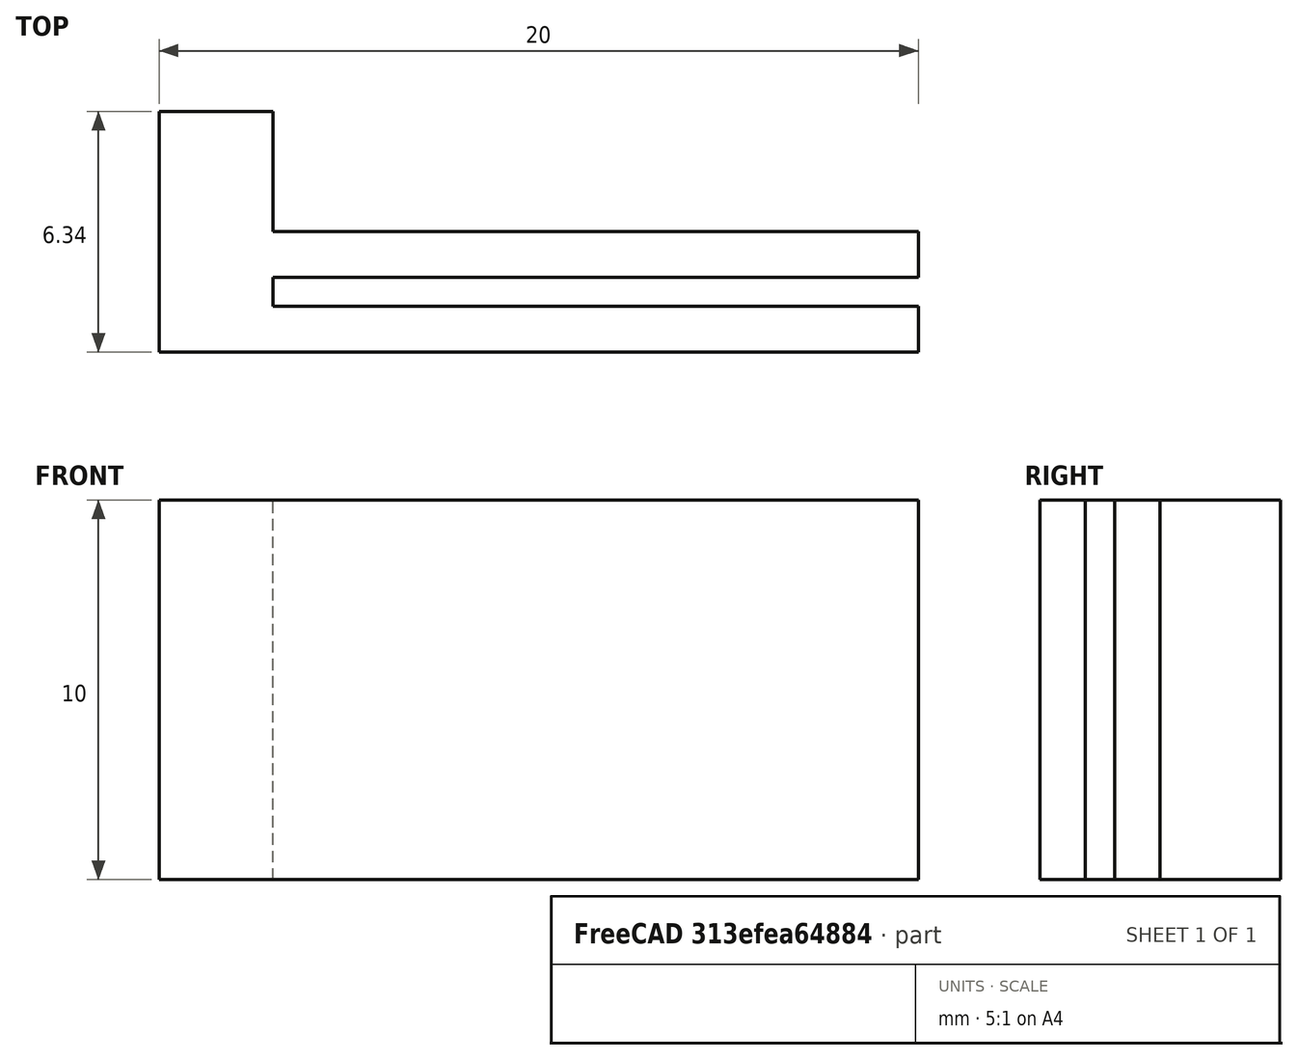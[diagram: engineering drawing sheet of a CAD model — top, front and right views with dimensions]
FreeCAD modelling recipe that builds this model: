
FCSTD DOCUMENT  (FreeCAD 0.22R38261 (Git))
Label: пазик для тубуса
License: All rights reserved
LicenseURL: https://en.wikipedia.org/wiki/All_rights_reserved
objects: Sketcher::SketchObject×1, PartDesign::Pad×1, PartDesign::Body×1
note: 5 computed .brp shape members not serialized (recipe doc carries the construction recipe); baked Part::Feature solids carry a one-line shape summary decoded from their .brp

FEATURE [Sketcher::SketchObject] Sketch
  AttachmentSupport = -> [XY_Plane]
  FullyConstrained = true
  MapMode = 5
  expr: Constraints[26] = 1.2 + 1.2 + 0.77
  sketch-geometry (10):
    g0: LineSegment StartX=0 StartY=0 StartZ=0 EndX=20 EndY=0 EndZ=0
    g1: LineSegment StartX=20 StartY=0 StartZ=0 EndX=20 EndY=1.2 EndZ=0
    g2: LineSegment StartX=20 StartY=1.2 StartZ=0 EndX=3 EndY=1.2 EndZ=0
    g3: LineSegment StartX=3 StartY=1.2 StartZ=0 EndX=3 EndY=1.97 EndZ=0
    g4: LineSegment StartX=3 StartY=1.97 StartZ=0 EndX=20 EndY=1.97 EndZ=0
    g5: LineSegment StartX=20 StartY=1.97 StartZ=0 EndX=20 EndY=3.17 EndZ=0
    g6: LineSegment StartX=20 StartY=3.17 StartZ=0 EndX=3 EndY=3.17 EndZ=0
    g7: LineSegment StartX=3 StartY=3.17 StartZ=0 EndX=3 EndY=6.34 EndZ=0
    g8: LineSegment StartX=3 StartY=6.34 StartZ=0 EndX=0 EndY=6.34 EndZ=0
    g9: LineSegment StartX=0 StartY=6.34 StartZ=0 EndX=0 EndY=0 EndZ=0
  constraints (29):
    c: Coincident(g0,g-1)
    c: PointOnObject(g0,g-1)
    c: Coincident(g1,g0)
    c: Vertical(g1)
    c: Horizontal(g2)
    c: Vertical(g3)
    c: Horizontal(g4)
    c: Coincident(g5,g4)
    c: Horizontal(g6)
    c: Vertical(g7)
    c: PointOnObject(g8,g-2)
    c: Coincident(g9,g8)
    c: Coincident(g9,g0)
    c: Coincident(g6,g7)
    c: Coincident(g7,g8)
    c: Coincident(g2,g3)
    c: Coincident(g3,g4)
    c: Coincident(g5,g6)
    c: Coincident(g1,g2)
    c: Vertical(g5)
    c: Equal(g1,g5)
    c: Vertical(g4,g1)
    c: Vertical(g6,g3)
    c: Horizontal(g8)
    c: DistanceY(g1,g4) = 0.77
    c: DistanceY(g4,g5) = 1.2
    c: DistanceY(g7,g7) = 3.17
    c: DistanceX(g0,g0) = 20
    c: DistanceX(g8,g8) = 3
FEATURE [PartDesign::Pad] Pad
  Direction = (0,0,1)
  Length = 10
  Length2 = 10
  Profile = -> Sketch
  ReferenceAxis = -> Sketch [N_Axis]
  Suppressed = false
  Type = 0
FEATURE [PartDesign::Body] Body  label="Тело"
  AllowCompound = false
  Group = -> [Sketch,Pad]
  Origin = -> Origin
  Tip = -> Pad
